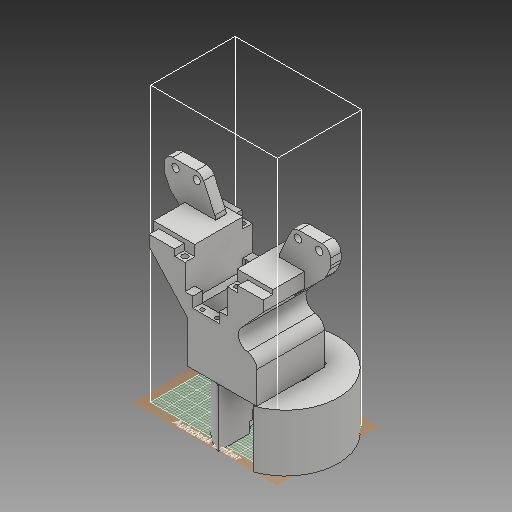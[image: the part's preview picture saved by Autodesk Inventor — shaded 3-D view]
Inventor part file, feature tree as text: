
AUTODESK INVENTOR PART (.ipt)
format: ipt  version: 2018 (Build 220112000, 112)  size: 968,192 bytes
history: native  units: mm
features: extrude x28, sketch x25, plane x6, mirror x5, fillet x5
ambient origin geometry x8: Origin, YZ Plane, XZ Plane, XY Plane, X Axis, Y Axis, Z Axis, Center Point
bodies: Solid1 (feature_tree)
feature tree (69):
  extrude  "base"  Depth=32.0mm
  extrude  "servo_place"  Depth=11.5mm
  plane  "Work Plane1"
  extrude  "pilars_top"  Depth=6.25mm
  extrude  "base_top"  Depth=12.5mm
  extrude  "screw_hole"  Depth=15.0mm TaperAngle=0.0deg
  plane  "Work Plane2"
  plane  "Work Plane6"
  plane  "Work Plane5"
  extrude  "Extrusion16"  Depth=18.0mm
  plane  "Work Plane3"
  plane  "Work Plane4"
  mirror  "Mirror1"
  mirror  "Mirror2"
  extrude  "Extrusion18"  Depth=5.0mm TaperAngle=0.0deg
  extrude  "Extrusion19"  Depth=2.5mm
  extrude  "Extrusion20"  Depth=5.0mm
  mirror  "Mirror3"
  mirror  "Mirror4"
  extrude  "Extrusion21"  Depth=25.0mm
  extrude  "Extrusion22"  [1 undecoded]
  extrude  "Extrusion23"  Depth=5.0mm
  extrude  "Extrusion11"  Depth=20.0mm
  extrude  "Extrusion24"  Depth=5.0mm
  fillet  "Fillet5"  Radius=30.0mm
  mirror  "Mirror5"
  extrude  "Extrusion25"  Depth=2.5mm
  extrude  "Extrusion26"  Depth=2.5mm
  extrude  "Extrusion27"  Depth=12.5mm
  fillet  "Fillet6"  Radius=12.5mm
  extrude  "Extrusion28"  Depth=12.5mm
  extrude  "Extrusion29"  Depth=7.0mm
  extrude  "Extrusion32"  Depth=27.0mm
  extrude  "Extrusion33"  Depth=10.0mm TaperAngle=0.0deg
  extrude  "Extrusion34"  Depth=3.5mm
  extrude  "Extrusion35"  Depth=3.5mm
  extrude  "Extrusion36"  Depth=15.0mm
  extrude  "Extrusion37"  Depth=1.0mm
  extrude  "Extrusion38"  Depth=18.0mm
  extrude  "Extrusion39"  Depth=8.0mm
  fillet  "Fillet10"  Radius=6.0mm
  fillet  "Fillet11"  Radius=5.0mm
  fillet  "Fillet12"  Radius=4.0mm
  extrude  "Extrusion40"  Depth=11.5mm
  sketch  "Sketch1"  dims[d0=18.0mm d1=32.0mm]
  sketch  "Sketch2"  dims[d2=25.0mm d3=0.0mm d4=11.5mm]
  sketch  "Sketch6"  dims[d5=90.0deg d6=6.25mm]
  sketch  "Sketch9"  dims[d7=23.0mm d8=12.5mm]
  sketch  "Sketch18"  dims[d9=22.0mm d10=0.0mm d26=15.0mm d27=0.0mm]
  sketch  "Sketch19"  dims[d39=18.0mm d40=18.0mm]
  sketch  "Sketch20"  dims[d41=5.0mm d42=0.0mm d47=5.0mm d48=0.0mm]
  sketch  "Sketch21"  dims[d55=5.0mm d56=0.0mm d60=2.5mm]
  sketch  "Sketch22"  dims[d61=5.0mm d62=5.0mm]
  sketch  "Sketch23"  dims[d63=-10.0mm d95=25.0mm]
  sketch  "Sketch24"  dims[d96=4.6mm d97=0.0mm d98=-16.0mm]
  sketch  "Sketch25"  dims[d100=12.5mm d105=5.0mm]
  sketch  "Sketch26"  dims[d106=10.0mm d107=20.0mm]
  sketch  "Sketch27"  dims[d108=10.0mm d109=0.0mm d110=5.0mm d111=30.0mm]
  sketch  "Sketch28"  dims[d112=3.0mm d113=0.0mm d114=2.5mm]
  sketch  "Sketch29"  dims[d115=2.5mm d116=2.8mm]
  sketch  "Sketch32"  dims[d117=5.0mm d118=0.0mm d119=11.75mm d120=12.5mm]
  sketch  "Sketch33"  dims[d121=23.5mm d122=12.5mm]
  sketch  "Sketch34"  dims[d123=10.0mm d124=0.0mm d125=7.0mm]
  sketch  "Sketch35"  dims[d126=10.0mm d127=0.0mm d131=27.0mm]
  sketch  "Sketch36"  dims[d132=27.0mm d133=10.0mm d134=0.0mm]
  sketch  "Sketch37"  dims[d135=10.0mm d137=3.5mm]
  sketch  "Sketch38"  dims[d138=10.0mm d139=3.5mm]
  sketch  "Sketch39"  dims[d140=3.0mm d141=15.0mm]
  sketch  "Sketch40"  dims[d142=27.052603mm d143=1.0mm d144=18.0mm d145=8.0mm d146=6.0mm d147=5.0mm d148=0.0mm d149=4.0mm d150=11.5mm d151=23.0mm d152=5.0mm d153=0.0mm d154=15.0mm d155=0.0mm d156=3.0mm d157=12.5mm d158=12.5mm d159=90.0deg d160=25.0mm d161=90.0deg d162=12.5mm d163=18.0mm d164=0.0mm d165=5.0mm d166=1.8mm d167=90.0deg d168=2.0mm d169=1.8mm d170=90.0deg d171=2.0mm d172=18.0mm d173=0.0mm d174=7.0mm d175=18.0mm d176=0.0mm d177=7.5mm d178=90.0deg d179=50.0mm d180=55.0mm d187=90.0deg d190=7.5mm d191=90.0deg d192=19.4mm d193=50.0mm d194=18.0mm d195=0.0mm d196=24.4mm d197=50.0mm d198=9.0mm d199=0.0mm d200=2.5mm d201=3.5mm d202=0.0mm d203=7.0mm d204=2.0mm d205=2.0mm d206=9.0mm d207=0.0mm d208=2.5mm d209=3.5mm d210=7.0mm d211=2.0mm d212=2.0mm d213=9.0mm d214=0.0mm d215=10.0mm d216=0.0mm d217=22.0mm d218=4.0mm d219=0.0mm d221=35.4mm d222=15.0mm d223=32.968414mm d224=2.0mm d225=10.0mm d226=0.0mm d227=1.0mm d228=24.4mm d229=24.0mm d230=12.0mm d231=1.5mm d232=1.5mm d233=1.5mm d234=1.5mm d235=10.0mm d236=0.0mm d238=1.5mm d239=1.5mm d241=1.0mm d243=1.0mm d245=4.0mm d246=2.0mm d247=2.0mm d248=3.5mm d249=10.0mm d250=0.0mm]
note: 1 required parameter value undecoded (feature->parameter linkage not recoverable at this tier; creation-order binding heuristic only, values carry confidence <= 0.55)
